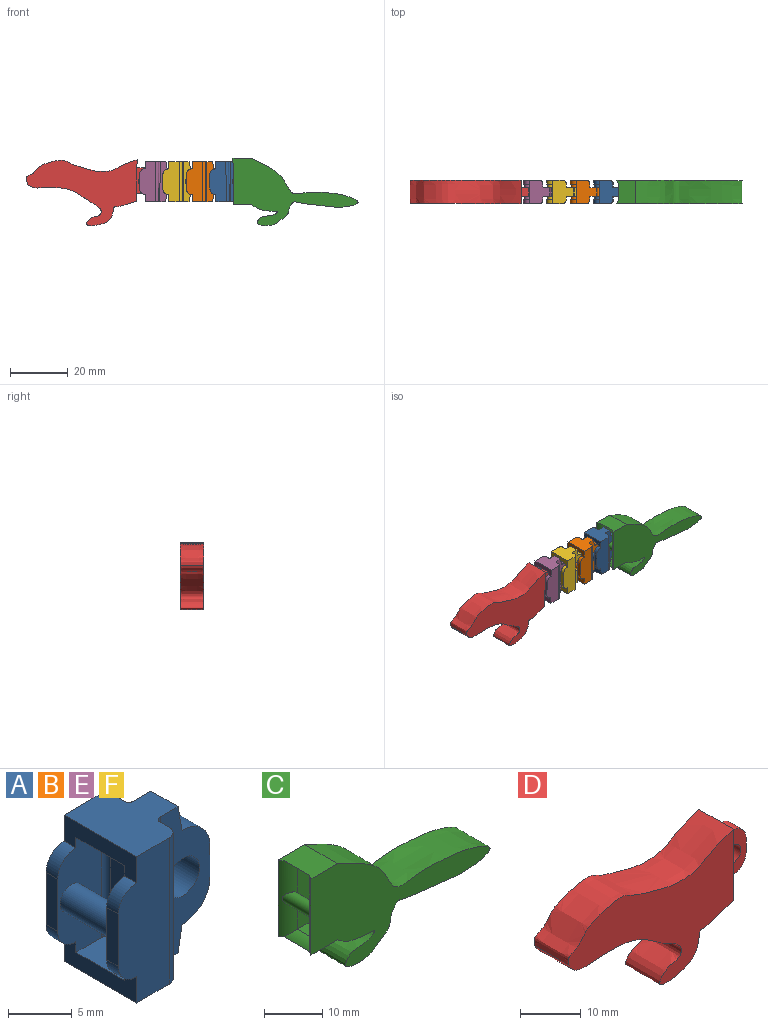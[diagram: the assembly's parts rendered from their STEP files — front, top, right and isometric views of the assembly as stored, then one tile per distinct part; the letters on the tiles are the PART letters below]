
ASSEMBLY  parts=6 mates=5
PART A: 34 faces, bbox 12.6x8x14 mm
  f0: plane 11x4.84mm, normal (0,-1,0), area 42.6mm2, adj f11,f16,f20,f23,f25,f26,f28,f29
  f1: plane 11x4.4mm, normal (-1,0,0), area 48.4mm2, adj f16,f18,f28,f30
  f2: plane 11x4.84mm, normal (0,1,0), area 42.6mm2, adj f3,f18,f20,f22,f24,f26,f28,f29
  f3: plane 5x1.3mm, normal (-1,0,0), area 6.5mm2, adj f2,f4,f22,f24
  f4: plane 14x5.64mm, normal (0,-1,0), area 67.2mm2, adj f3,f15,f22,f24,f26,f27,f29,f31
  f5: plane 14x1mm, normal (1,0,0), area 14mm2, adj f15,f19,f27,f31
  f6: plane 14x5.49mm, normal (0,-1,0), area 46.3mm2, adj f7,f12,f13,f19,f21,f27,f31,f32
  f7: plane 3x3mm, normal (1,0,0), area 9mm2, adj f6,f8,f12,f13
  f8: plane 14x5.49mm, normal (0,1,0), area 46.3mm2, adj f7,f12,f13,f17,f21,f27,f31,f32
  f9: plane 14x1mm, normal (1,0,0), area 14mm2, adj f14,f17,f27,f31
  f10: plane 14x5.64mm, normal (0,1,0), area 67.2mm2, adj f11,f14,f23,f25,f26,f27,f29,f31
  f11: plane 5x1.3mm, normal (-1,0,0), area 6.5mm2, adj f0,f10,f23,f25
  f12: cylinder r=3mm len=3.09mm, axis (0,1,0), area 14.4mm2, adj f6,f7,f8,f32
  f13: cylinder r=3mm len=3.09mm, axis (0,-1,0), area 14.4mm2, adj f6,f7,f8,f33
  f14: cylinder r=1mm len=14mm, axis (0,0,-1), area 22mm2, adj f9,f10,f27,f31
  f15: cylinder r=1mm len=14mm, axis (0,0,-1), area 22mm2, adj f4,f5,f27,f31
  f16: cylinder r=0.5mm len=11mm, axis (0,0,1), area 8.6mm2, adj f0,f1,f28,f30
  f17: cylinder r=0.5mm len=14mm, axis (0,0,1), area 11mm2, adj f8,f9,f27,f31
  f18: cylinder r=0.5mm len=11mm, axis (0,0,-1), area 8.6mm2, adj f1,f2,f28,f30
  f19: cylinder r=0.5mm len=14mm, axis (0,0,1), area 11mm2, adj f5,f6,f27,f31
  f20: cylinder r=1.25mm len=5.4mm, axis (0,-1,0), area 42.4mm2, adj f0,f2
  f21: cylinder r=1.8mm len=3.6mm, axis (0,1,0), area 33.9mm2, adj f6,f8
  f22: cylinder r=2mm len=2mm, axis (0,-1,0), area 4.1mm2, adj f2,f3,f4,f29
  f23: cylinder r=2mm len=2mm, axis (0,-1,0), area 4.1mm2, adj f0,f10,f11,f29
  f24: cylinder r=2mm len=2mm, axis (0,1,0), area 4.1mm2, adj f2,f3,f4,f26
  f25: cylinder r=2mm len=2mm, axis (0,1,0), area 4.1mm2, adj f0,f10,f11,f26
  f26: plane 8x2.5mm, normal (-1,0,0), area 14.6mm2, adj f0,f2,f4,f10,f24,f25,f27,f28
  f27: plane 8x7.1mm, normal (0,0,1), area 44.2mm2, adj f4,f5,f6,f8,f9,f10,f14,f15
  f28: plane 5.4x3.34mm, normal (0,0,-1), area 17.9mm2, adj f0,f1,f2,f16,f18,f26
  f29: plane 8x2.5mm, normal (-1,0,0), area 14.6mm2, adj f0,f2,f4,f10,f22,f23,f30,f31
  f30: plane 5.4x3.34mm, normal (0,0,1), area 17.9mm2, adj f0,f1,f2,f16,f18,f29
  f31: plane 8x7.1mm, normal (0,0,-1), area 44.2mm2, adj f4,f5,f6,f8,f9,f10,f14,f15
  f32: plane 3x2.5mm, normal (0.98,0,-0.17), area 7.6mm2, adj f6,f8,f12,f31
  f33: plane 3x2.5mm, normal (0.98,0,0.17), area 7.6mm2, adj f6,f8,f13,f27
PART B: same geometry as A
PART C: 15 faces, bbox 43.7x8x23.6 mm
  f0: extruded ~36.54x23.34mm, area 797mm2, adj f1,f2,f3,f4
  f1: plane 43.7x23.6mm, normal (0,-1,0), area 411mm2, adj f0,f3,f4,f14
  f2: plane 43.7x23.6mm, normal (0,1,0), area 411mm2, adj f0,f3,f4,f11
  f3: plane 8x6.43mm, normal (0,0,1), area 47.6mm2, adj f0,f1,f2,f11,f12,f14
  f4: plane 8x6.43mm, normal (0,0,-1), area 47.6mm2, adj f0,f1,f2,f11,f13,f14
  f5: plane 4.18x3.64mm, normal (0,0,1), area 15.2mm2, adj f6,f8,f9,f13
  f6: plane 14x3.64mm, normal (0,-1,0), area 50.9mm2, adj f5,f7,f9,f10,f11
  f7: plane 4.18x3.64mm, normal (0,0,-1), area 15.2mm2, adj f6,f8,f9,f12
  f8: plane 14x3.64mm, normal (0,1,0), area 50.9mm2, adj f5,f7,f9,f10,f14
  f9: plane 14x4.18mm, normal (-1,0,0), area 58.5mm2, adj f5,f6,f7,f8
  f10: cylinder r=1.25mm len=6.7mm, axis (0,1,0), area 39.6mm2, adj f6,f8,f11,f14
  f11: cylinder r=3mm len=16mm, axis (0,0,-1), area 48.7mm2, adj f2,f3,f4,f6,f10,f12,f13
  f12: cylinder r=3mm len=6.18mm, axis (0,1,0), area 12.3mm2, adj f3,f7,f11,f14
  f13: cylinder r=3mm len=6.18mm, axis (0,-1,0), area 12.3mm2, adj f4,f5,f11,f14
  f14: cylinder r=3mm len=16mm, axis (0,0,1), area 48.7mm2, adj f1,f3,f4,f8,f10,f12,f13
PART D: 13 faces, bbox 44.1x8x23.5 mm
  f0: extruded ~38.49x8.38mm, area 346.9mm2, adj f1,f2,f3,f4
  f1: extruded ~38.31x14.84mm, area 464.4mm2, adj f0,f2,f3,f4
  f2: plane 14.46x8mm, normal (1,0,0), area 88.7mm2, adj f0,f1,f3,f4,f5,f6,f7,f8
  f3: plane 38.57x23.46mm, normal (0,-1,0), area 432.5mm2, adj f0,f1,f2
  f4: plane 38.57x23.46mm, normal (0,1,0), area 432.5mm2, adj f0,f1,f2
  f5: plane 3x2.49mm, normal (0,0,1), area 7.5mm2, adj f2,f6,f8,f11
  f6: plane 9x5.49mm, normal (0,-1,0), area 35.4mm2, adj f2,f5,f7,f9,f10,f11,f12
  f7: plane 3x2.49mm, normal (0,0,-1), area 7.5mm2, adj f2,f6,f8,f10
  f8: plane 9x5.49mm, normal (0,1,0), area 35.4mm2, adj f2,f5,f7,f9,f10,f11,f12
  f9: plane 3x3mm, normal (1,0,0), area 9mm2, adj f6,f8,f10,f11
  f10: cylinder r=3mm len=3mm, axis (0,-1,0), area 14.1mm2, adj f6,f7,f8,f9
  f11: cylinder r=3mm len=3mm, axis (0,1,0), area 14.1mm2, adj f5,f6,f8,f9
  f12: cylinder r=1.8mm len=3.6mm, axis (0,-1,0), area 33.9mm2, adj f6,f8
PART E: same geometry as A
PART F: same geometry as A
PLACE A rot(axis=(0,-1,0),0.8deg) t=(16.32,0,0)mm
PLACE B t=(8.16,0,0)mm
PLACE C rot(axis=(0,-1,0),0.1deg) t=(22.97,4,-3.87)mm
PLACE D rot(axis=(0,1,0),1.2deg) t=(-22.49,4,-0.98)mm
PLACE E rot(axis=(0,1,0),0.7deg) t=(-8.16,0,0.1)mm
PLACE F at identity fixed
MATE revolute A.f20 <-> B.f21  axis (0,-1,0) through (16.32,0,0)mm
MATE revolute D.f12 <-> E.f20  axis (0,-1,0) through (-8.16,0,0.1)mm
MATE revolute A.f21 <-> C.f10  axis (0,1,0) through (24.48,0,0.11)mm
MATE revolute B.f20 <-> F.f21  axis (0,-1,0) through (8.16,0,0)mm
MATE revolute E.f21 <-> F.f20  axis (0,1,0) through (0,0,0)mm
